# Revit family: TMX
name_source: partatom
category: Mechanical Equipment
units: mm (PartAtom-declared; Revit-internal decimal feet)

## family parameters
Always vertical = Yes
Cut with Voids When Loaded = No
Part Type = Normal
Room Calculation Point = No
Round Connector Dimension = Use Radius
Shared = No
Work Plane-Based = No

## types (12) — shared parameters
0 = 0"
1.5 = 1 1/2"
1.9375 = 1 15/16"
3 = 3"
45 = 45.00°
BRACKET = 3"
BRACKET/2 = 1 1/2"
H = 1/2"
H/2 = 1/4"
Manufacturer = Loren Cook Company
Model = TMX-Horizontal
ONE EIGTH = 1/8"
Type Comments = Mixed Flow Inline Horizontal Mount Belt Drive Arrangement 9
URL = www.lorencook.com

## per-type parameters (varying)
- 90-TMX: (A/2)-.125=6 5/16"; (F+3)/2=8 5/8"; (F/2)+1.5=8 5/8"; (F/2)-1.5=5 5/8"; (G/2)+1.5=9 9/16"; (G/2)-.75=7 5/16"; (G/2)-1.5=6 9/16"; -(B/2)=-9 1/4"; -(G/2)-.75=-7 5/16"; A=12 7/8"; A/2=6 7/16"; A/4=3 7/32"; A/8=2 5/32"; B=18 1/2"; B/10=1 27/32"; B/2=9 1/4"; B/3*2=12 11/32"; B/6=3 3/32"; B/8=3 3/32"; C=15 7/8"; C/2=7 15/16"; D=9 3/8"; E=29 1/16"; E-D=19 11/16"; E-D-1.5=18 3/16"; F=14 1/4"; F+1.5=15 3/4"; F-1.5=12 3/4"; F/2=7 1/8"; G=16 1/8"; G+1.5=17 5/8"; G/2=8 1/16"; MC/2=5 1/8"; hole=6 13/32"; hole_dia=18 1/8"
- 120-TMX: (A/2)-.125=8 7/16"; (F+3)/2=9 1/4"; (F/2)+1.5=9 1/4"; (F/2)-1.5=6 1/4"; (G/2)+1.5=12 21/32"; (G/2)-.75=10 13/32"; (G/2)-1.5=9 21/32"; -(B/2)=-12 11/32"; -(G/2)-.75=-10 13/32"; A=17 1/8"; A/2=8 9/16"; A/4=4 9/32"; A/8=2 27/32"; B=24 11/16"; B/10=2 15/32"; B/2=12 11/32"; B/3*2=16 15/32"; B/6=4 1/8"; B/8=4 1/8"; C=20 1/16"; C/2=10 1/32"; D=11 11/16"; E=33 3/4"; E-D=22 1/16"; E-D-1.5=20 9/16"; F=15 1/2"; F+1.5=17"; F-1.5=14"; F/2=7 3/4"; G=22 5/16"; G+1.5=23 13/16"; G/2=11 5/32"; MC/2=5 3/4"; hole=7 31/32"; hole_dia=22 9/16"
- 135-TMX: (A/2)-.125=9 15/32"; (F+3)/2=10 31/32"; (F/2)+1.5=10 31/32"; (F/2)-1.5=7 31/32"; (G/2)+1.5=14 3/16"; (G/2)-.75=11 15/16"; (G/2)-1.5=11 3/16"; -(B/2)=-13 7/8"; -(G/2)-.75=-11 15/16"; A=19 3/16"; A/2=9 19/32"; A/4=4 13/16"; A/8=3 3/16"; B=27 3/4"; B/10=2 25/32"; B/2=13 7/8"; B/3*2=18 1/2"; B/6=4 5/8"; B/8=4 5/8"; C=22 1/4"; C/2=11 1/8"; D=11 11/16"; E=35 1/2"; E-D=23 13/16"; E-D-1.5=22 5/16"; F=18 15/16"; F+1.5=20 7/16"; F-1.5=17 7/16"; F/2=9 15/32"; G=25 3/8"; G+1.5=26 7/8"; G/2=12 11/16"; MC/2=7 15/32"; hole=8 3/4"; hole_dia=24 3/4"
- 150-TMX: (A/2)-.125=10 17/32"; (F+3)/2=11 23/32"; (F/2)+1.5=11 23/32"; (F/2)-1.5=8 23/32"; (G/2)+1.5=14 5/16"; (G/2)-.75=12 1/16"; (G/2)-1.5=11 5/16"; -(B/2)=-14"; -(G/2)-.75=-12 1/16"; A=21 5/16"; A/2=10 21/32"; A/4=5 11/32"; A/8=3 9/16"; B=28"; B/10=2 13/16"; B/2=14"; B/3*2=18 21/32"; B/6=4 21/32"; B/8=4 21/32"; C=24 3/8"; C/2=12 3/16"; D=12 7/16"; E=37 5/16"; E-D=24 7/8"; E-D-1.5=23 3/8"; F=20 7/16"; F+1.5=21 15/16"; F-1.5=18 15/16"; F/2=10 7/32"; G=25 5/8"; G+1.5=27 1/8"; G/2=12 13/16"; MC/2=8 7/32"; hole=9 1/2"; hole_dia=26 7/8"
- 165-TMX: (A/2)-.125=11 19/32"; (F+3)/2=12 9/16"; (F/2)+1.5=12 9/16"; (F/2)-1.5=9 9/16"; (G/2)+1.5=15 23/32"; (G/2)-.75=13 15/32"; (G/2)-1.5=12 23/32"; -(B/2)=-15 13/32"; -(G/2)-.75=-13 15/32"; A=23 7/16"; A/2=11 23/32"; A/4=5 7/8"; A/8=3 29/32"; B=30 13/16"; B/10=3 3/32"; B/2=15 13/32"; B/3*2=20 17/32"; B/6=5 1/8"; B/8=5 1/8"; C=26 1/2"; C/2=13 1/4"; D=13 9/16"; E=39 1/2"; E-D=25 15/16"; E-D-1.5=24 7/16"; F=22 1/8"; F+1.5=23 5/8"; F-1.5=20 5/8"; F/2=11 1/16"; G=28 7/16"; G+1.5=29 15/16"; G/2=14 7/32"; MC/2=9 1/16"; hole=10 11/32"; hole_dia=29 1/4"
- 180-TMX: (A/2)-.125=12 21/32"; (F+3)/2=13 5/16"; (F/2)+1.5=13 5/16"; (F/2)-1.5=10 5/16"; (G/2)+1.5=17 1/8"; (G/2)-.75=14 7/8"; (G/2)-1.5=14 1/8"; -(B/2)=-16 13/16"; -(G/2)-.75=-14 7/8"; A=25 9/16"; A/2=12 25/32"; A/4=6 13/32"; A/8=4 1/4"; B=33 5/8"; B/10=3 3/8"; B/2=16 13/16"; B/3*2=22 13/32"; B/6=5 19/32"; B/8=5 19/32"; C=28 5/8"; C/2=14 5/16"; D=14 5/8"; E=43 5/8"; E-D=29"; E-D-1.5=27 1/2"; F=23 5/8"; F+1.5=25 1/8"; F-1.5=22 1/8"; F/2=11 13/16"; G=31 1/4"; G+1.5=32 3/4"; G/2=15 5/8"; MC/2=9 13/16"; hole=11 3/32"; hole_dia=31 3/8"
- 202-TMX: (A/2)-.125=14 7/32"; (F+3)/2=14 13/32"; (F/2)+1.5=14 13/32"; (F/2)-1.5=11 13/32"; (G/2)+1.5=19 5/32"; (G/2)-.75=16 29/32"; (G/2)-1.5=16 5/32"; -(B/2)=-18 27/32"; -(G/2)-.75=-16 29/32"; A=28 11/16"; A/2=14 11/32"; A/4=7 3/16"; A/8=4 25/32"; B=37 11/16"; B/10=3 25/32"; B/2=18 27/32"; B/3*2=25 1/8"; B/6=6 9/32"; B/8=6 9/32"; C=31 3/4"; C/2=15 7/8"; D=16 1/8"; E=46 11/16"; E-D=30 9/16"; E-D-1.5=29 1/16"; F=25 13/16"; F+1.5=27 5/16"; F-1.5=24 5/16"; F/2=12 29/32"; G=35 5/16"; G+1.5=36 13/16"; G/2=17 21/32"; MC/2=10 29/32"; hole=12 3/16"; hole_dia=34 1/2"
- 225-TMX: (A/2)-.125=15 27/32"; (F+3)/2=15 5/8"; (F/2)+1.5=15 5/8"; (F/2)-1.5=12 5/8"; (G/2)+1.5=21 5/16"; (G/2)-.75=19 1/16"; (G/2)-1.5=18 5/16"; -(B/2)=-21"; -(G/2)-.75=-19 1/16"; A=31 15/16"; A/2=15 31/32"; A/4=8"; A/8=5 5/16"; B=42"; B/10=4 3/16"; B/2=21"; B/3*2=28"; B/6=7"; B/8=7"; C=34 15/16"; C/2=17 15/32"; D=17 3/4"; E=49 15/16"; E-D=32 3/16"; E-D-1.5=30 11/16"; F=28 1/4"; F+1.5=29 3/4"; F-1.5=26 3/4"; F/2=14 1/8"; G=39 5/8"; G+1.5=41 1/8"; G/2=19 13/16"; MC/2=12 1/8"; hole=13 13/32"; hole_dia=37 15/16"
- 245-TMX: (A/2)-.125=17 1/4"; (F+3)/2=17 5/16"; (F/2)+1.5=17 5/16"; (F/2)-1.5=14 5/16"; (G/2)+1.5=22 1/2"; (G/2)-.75=20 1/4"; (G/2)-1.5=19 1/2"; -(B/2)=-22 1/4"; -(G/2)-.75=-20 1/4"; A=34 3/4"; A/2=17 3/8"; A/4=8 11/16"; A/8=5 25/32"; B=44 1/2"; B/10=4 7/16"; B/2=22 1/4"; B/3*2=29 21/32"; B/6=7 13/32"; B/8=7 13/32"; C=38 3/4"; C/2=19 3/8"; D=21 7/16"; E=57 1/16"; E-D=35 5/8"; E-D-1.5=34 1/8"; F=31 5/8"; F+1.5=33 1/8"; F-1.5=30 1/8"; F/2=15 13/16"; G=42"; G+1.5=43 1/2"; G/2=21"; MC/2=13 13/16"; hole=15 1/8"; hole_dia=42 3/4"
- 270-TMX: (A/2)-.125=19"; (F+3)/2=18 19/32"; (F/2)+1.5=18 19/32"; (F/2)-1.5=15 19/32"; (G/2)+1.5=24 25/32"; (G/2)-.75=22 17/32"; (G/2)-1.5=21 25/32"; -(B/2)=-24 17/32"; -(G/2)-.75=-22 17/32"; A=38 1/4"; A/2=19 1/8"; A/4=9 9/16"; A/8=6 3/8"; B=49 1/16"; B/10=4 29/32"; B/2=24 17/32"; B/3*2=32 23/32"; B/6=8 3/16"; B/8=8 3/16"; C=42 3/8"; C/2=21 3/16"; D=22 11/16"; E=60 1/16"; E-D=37 3/8"; E-D-1.5=35 7/8"; F=34 3/16"; F+1.5=35 11/16"; F-1.5=32 11/16"; F/2=17 3/32"; G=46 9/16"; G+1.5=48 1/16"; G/2=23 9/32"; MC/2=15 3/32"; hole=16 3/8"; hole_dia=46 5/16"
- 300-TMX: (A/2)-.125=21 1/8"; (F+3)/2=20 1/16"; (F/2)+1.5=20 1/16"; (F/2)-1.5=17 1/16"; (G/2)+1.5=27 1/2"; (G/2)-.75=25 1/4"; (G/2)-1.5=24 1/2"; -(B/2)=-27 1/4"; -(G/2)-.75=-25 1/4"; A=42 1/2"; A/2=21 1/4"; A/4=10 5/8"; A/8=7 3/32"; B=54 1/2"; B/10=5 7/16"; B/2=27 1/4"; B/3*2=36 11/32"; B/6=9 3/32"; B/8=9 3/32"; C=46 1/2"; C/2=23 1/4"; D=24 3/16"; E=63 11/16"; E-D=39 1/2"; E-D-1.5=38"; F=37 1/8"; F+1.5=38 5/8"; F-1.5=35 5/8"; F/2=18 9/16"; G=52"; G+1.5=53 1/2"; G/2=26"; MC/2=16 9/16"; hole=17 27/32"; hole_dia=50 1/2"
- 330-TMX: (A/2)-.125=23 7/32"; (F+3)/2=21 9/16"; (F/2)+1.5=21 9/16"; (F/2)-1.5=18 9/16"; (G/2)+1.5=30 7/32"; (G/2)-.75=27 31/32"; (G/2)-1.5=27 7/32"; -(B/2)=-29 31/32"; -(G/2)-.75=-27 31/32"; A=46 11/16"; A/2=23 11/32"; A/4=11 11/16"; A/8=7 25/32"; B=59 15/16"; B/10=6"; B/2=29 31/32"; B/3*2=39 31/32"; B/6=10"; B/8=10"; C=50 3/4"; C/2=25 3/8"; D=25 11/16"; E=67 3/8"; E-D=41 11/16"; E-D-1.5=40 3/16"; F=40 1/8"; F+1.5=41 5/8"; F-1.5=38 5/8"; F/2=20 1/16"; G=57 7/16"; G+1.5=58 15/16"; G/2=28 23/32"; MC/2=18 1/16"; hole=19 11/32"; hole_dia=54 3/4"

## geometry (parser evidence)
native form markers: Sweep x2
no freeform markers — native parametric forms only
